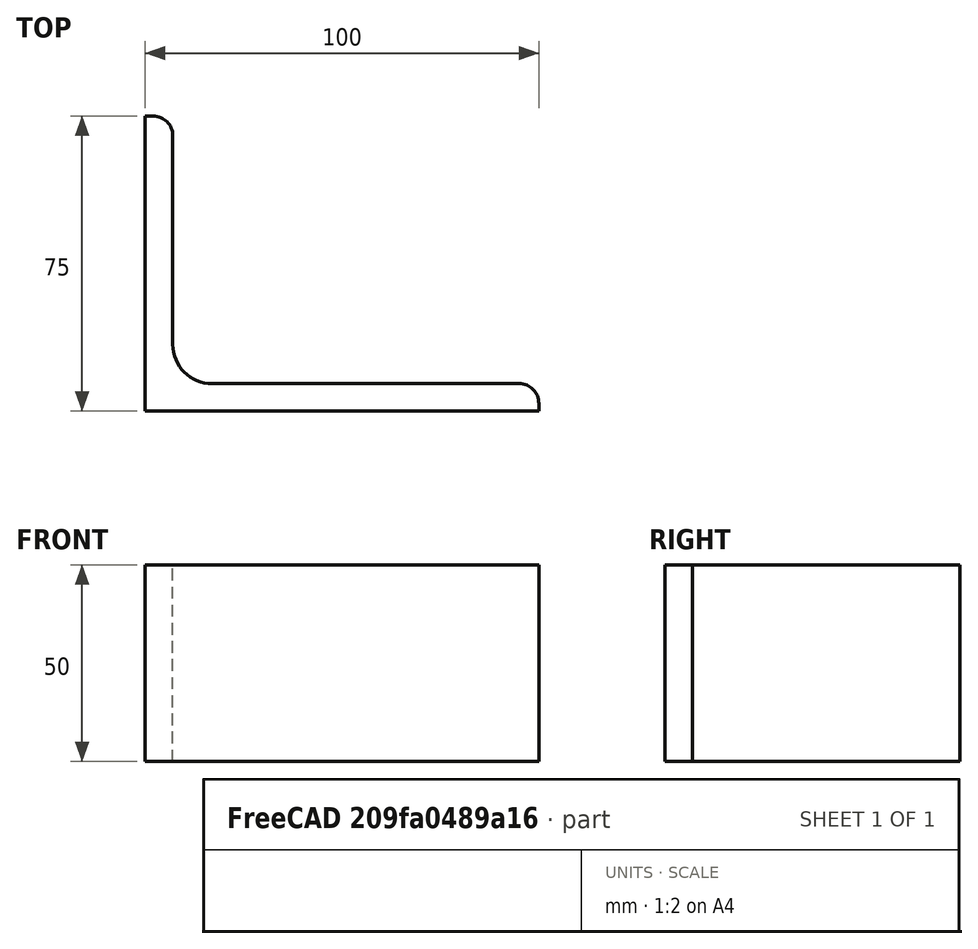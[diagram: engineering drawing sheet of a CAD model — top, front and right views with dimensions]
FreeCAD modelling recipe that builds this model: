
FCSTD DOCUMENT  (FreeCAD 0.15R4671 (Git))
Label: Angle Bar 100x75x7 EN10056 S235JR
License: All rights reserved
LicenseURL: http://en.wikipedia.org/wiki/All_rights_reserved
objects: Sketcher::SketchObject×1, Part::Extrusion×1
note: 2 computed .brp shape members not serialized (recipe doc carries the construction recipe); baked Part::Feature solids carry a one-line shape summary decoded from their .brp

FEATURE [Sketcher::SketchObject] Sketch
  sketch-geometry (9):
    g0: LineSegment StartX=0 StartY=0 StartZ=0 EndX=100 EndY=0 EndZ=0
    g1: LineSegment StartX=100 StartY=0 StartZ=0 EndX=100 EndY=2 EndZ=0
    g2: LineSegment StartX=95 StartY=7 StartZ=0 EndX=17 EndY=7 EndZ=0
    g3: LineSegment StartX=0 StartY=0 StartZ=0 EndX=0 EndY=75 EndZ=0
    g4: LineSegment StartX=0 StartY=75 StartZ=0 EndX=2 EndY=75 EndZ=0
    g5: LineSegment StartX=7 StartY=70 StartZ=0 EndX=7 EndY=17 EndZ=0
    g6: ArcOfCircle CenterX=17 CenterY=17 CenterZ=0 NormalX=0 NormalY=0 NormalZ=1 Radius=10 StartAngle=3.14159 EndAngle=4.71239
    g7: ArcOfCircle CenterX=2 CenterY=70 CenterZ=0 NormalX=0 NormalY=0 NormalZ=1 Radius=5 StartAngle=0 EndAngle=1.5708
    g8: ArcOfCircle CenterX=95 CenterY=2 CenterZ=0 NormalX=0 NormalY=0 NormalZ=1 Radius=5 StartAngle=0 EndAngle=1.5708
  constraints (23):
    c: Coincident(g0,g-1)
    c: Horizontal(g0)
    c: Coincident(g1,g0)
    c: Vertical(g1)
    c: Horizontal(g2)
    c: Coincident(g3,g-1)
    c: Vertical(g3)
    c: Coincident(g4,g3)
    c: Horizontal(g4)
    c: Vertical(g5)
    c: Tangent(g5,g6) = -1.5708
    c: Tangent(g2,g6) = 1.5708
    c: Tangent(g4,g7) = 1.5708
    c: Tangent(g5,g7) = 1.5708
    c: Tangent(g2,g8) = -1.5708
    c: Tangent(g1,g8) = -1.5708
    c: DistanceX(g0) = 100
    c: DistanceY(g3) = 75
    c: DistanceY(g0,g2) = 7
    c: DistanceX(g3,g5) = 7
    c: Radius(g6) = 10
    c: Radius(g8) = 5
    c: Radius(g7) = 5
FEATURE [Part::Extrusion] Extrude  label="Angle Bar 100x75x7 EN10056 S235JR"
  Base = -> Sketch
  Dir = (0,0,50)
  Solid = true
